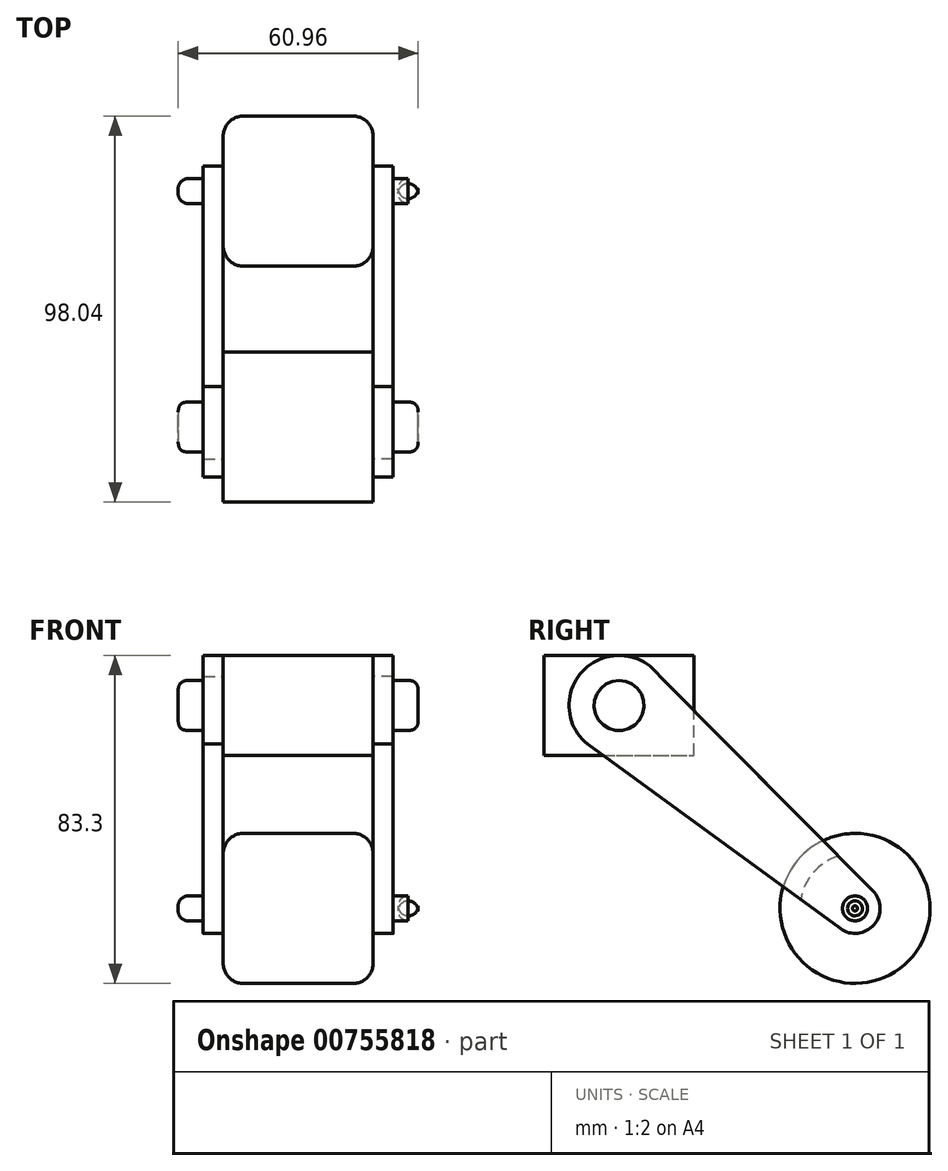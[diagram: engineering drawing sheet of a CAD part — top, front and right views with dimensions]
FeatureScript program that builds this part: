
annotation { "Feature Type Name" : "Feature", "Feature Type Description" : "" }
export const myFeature = defineFeature(function(context is Context, id is Id, definition is map)
    precondition{}
    {
        {
            var Q0;
            Q0=qCreatedBy(makeId("Right.planeOp"),FACE);
            var sketch = newSketch(context, id + "F0", { "sketchPlane" : qUnion([Q0])});
            skLineSegment(sketch, "E0.bottom", {"start": v(-59, 38.85) * mm, "end": v(-20.9, 38.85) * mm});
            skLineSegment(sketch, "E0.top", {"start": v(-59, 64.25) * mm, "end": v(-20.9, 64.25) * mm});
            skLineSegment(sketch, "E0.left", {"start": v(-59, 38.85) * mm, "end": v(-59, 64.25) * mm});
            skLineSegment(sketch, "E0.right", {"start": v(-20.9, 38.85) * mm, "end": v(-20.9, 64.25) * mm});
            skSolve(sketch);
        }
        {
            var Q0;
            Q0=makeQuery(id+"F0.imprint","IMPRINT",FACE,{"disambiguationData":[TD([[makeQuery(id+"F0.imprint","IMPRINT",EDGE,{"derivedFrom":sQuery(id+"F0.wireOp",EDGE,"E0.bottom")}),1.0]])]});
            extrude(context, id + "F1", {"entities" : qUnion([Q0]), "depth" : 19.05 * mm, "hasSecondDirection" : true, "secondDirectionOppositeDirection" : true, "secondDirectionDepth" : 19.05 * mm});
        }
        {
            var Q0;
            Q0=makeQuery(id+"F1.opExtrude","CAP_FACE",FACE,{"disambiguationData":[OSD([sQuery(id+"F0.wireOp",EDGE,"E0.bottom"),sQuery(id+"F0.wireOp",EDGE,"E0.top"),sQuery(id+"F0.wireOp",EDGE,"E0.left"),sQuery(id+"F0.wireOp",EDGE,"E0.right")])],"isStart":false});
            var sketch = newSketch(context, id + "F2", { "sketchPlane" : qUnion([Q0])});
            skArc(sketch, "E1", {"start": v(-29.6, 58.92) * mm, "mid": v(-48.61, 60.84) * mm, "end": v(-48.03, 41.75) * mm});
            skPoint(sketch, "E1.centerSnap0", {"position": v(-59, 51.55) * mm});
            skPoint(sketch, "E1.centerSnap1", {"position": v(-39.95, 38.85) * mm});
            skArc(sketch, "E2", {"start": v(16.24, -5.14) * mm, "mid": v(24.82, -4.14) * mm, "end": v(24.5, 4.48) * mm});
            skLineSegment(sketch, "E3", {"start": v(-29.6, 58.92) * mm, "end": v(24.5, 4.48) * mm});
            skLineSegment(sketch, "E4", {"start": v(-48.03, 41.75) * mm, "end": v(16.24, -5.14) * mm});
            skCircle(sketch, "E5", {"center": v(20, 0) * mm, "radius": 3.18 * mm});
            skSolve(sketch);
        }
        {
            var Q0;
            Q0=qSketchRegion(id+"F2",true);
            extrude(context, id + "F3", {"entities" : qUnion([Q0]), "depth" : 5.08 * mm});
        }
        {
            var Q0;
            Q0=makeQuery(id+"F3.opExtrude","CAP_FACE",FACE,{"disambiguationData":[OSD([sQuery(id+"F2.wireOp",EDGE,"E1"),sQuery(id+"F2.wireOp",EDGE,"E2"),sQuery(id+"F2.wireOp",EDGE,"E3"),sQuery(id+"F2.wireOp",EDGE,"E4")])],"isStart":true});
            cPlane(context, id + "F4", {"entities" : qUnion([Q0]), "cplaneType" : CPlaneType.OFFSET, "offset" : 19.05 * mm, "width" : 152.4 * mm, "height" : 152.4 * mm});
        }
        {
            var Q0;
            Q0=makeQuery(id+"F3.opExtrude","SWEPT_BODY",BODY,{"disambiguationData":[OSD([sQuery(id+"F2.wireOp",EDGE,"E1"),sQuery(id+"F2.wireOp",EDGE,"E2"),sQuery(id+"F2.wireOp",EDGE,"E3"),sQuery(id+"F2.wireOp",EDGE,"E4")])]});
            var Q1;
            Q1=qCreatedBy(id+"F4.planeOp",FACE);
            mirror(context, id + "F5", {"entities" : qUnion([Q0]), "mirrorPlane" : qUnion([Q1])});
        }
        {
            var Q0;
            Q0=makeQuery(id+"F3.opExtrude","CAP_FACE",FACE,{"disambiguationData":[OSD([sQuery(id+"F2.wireOp",EDGE,"E1"),sQuery(id+"F2.wireOp",EDGE,"E2"),sQuery(id+"F2.wireOp",EDGE,"E3"),sQuery(id+"F2.wireOp",EDGE,"E4")])],"isStart":true});
            var sketch = newSketch(context, id + "F6", { "sketchPlane" : qUnion([Q0])});
            skCircle(sketch, "E6", {"center": v(-20, 0) * mm, "radius": 19.05 * mm});
            skCircle(sketch, "E7", {"center": v(-20, 0) * mm, "radius": 3.18 * mm});
            skSolve(sketch);
        }
        {
            var Q0;
            Q0=qSketchRegion(id+"F6",true);
            extrude(context, id + "F7", {"entities" : qUnion([Q0]), "depth" : 38.1 * mm});
        }
        {
            var Q0;
            Q0=makeQuery(id+"F5.opPattern","COPY",FACE,{"derivedFrom":makeQuery(id+"F3.opExtrude","CAP_FACE",FACE,{"disambiguationData":[OSD([sQuery(id+"F2.wireOp",EDGE,"E1"),sQuery(id+"F2.wireOp",EDGE,"E2"),sQuery(id+"F2.wireOp",EDGE,"E3"),sQuery(id+"F2.wireOp",EDGE,"E4")])],"isStart":false}),"instanceName":"1"});
            var sketch = newSketch(context, id + "F8", { "sketchPlane" : qUnion([Q0])});
            skCircle(sketch, "E8", {"center": v(39.95, 51.55) * mm, "radius": 6.35 * mm});
            skSolve(sketch);
        }
        {
            var Q0;
            Q0=qSketchRegion(id+"F8",true);
            extrude(context, id + "F9", {"entities" : qUnion([Q0]), "depth" : 6.35 * mm});
        }
        {
            var Q0;
            Q0=makeQuery(id+"F9.opExtrude","CAP_FACE",FACE,{"disambiguationData":[OSD([sQuery(id+"F8.wireOp",EDGE,"E8")])],"isStart":false});
            fillet(context, id + "F10", {"entities" : qUnion([Q0]), "radius" : 2.54 * mm, "tangentPropagation" : true, "rho" : 0.5, "crossSection" : FilletCrossSection.CONIC, "allowEdgeOverflow" : false});
        }
        {
            var Q0;
            Q0=makeQuery(id+"F9.opExtrude","SWEPT_BODY",BODY,{"disambiguationData":[OSD([sQuery(id+"F8.wireOp",EDGE,"E8")])]});
            var Q1;
            Q1=qCreatedBy(id+"F4.planeOp",FACE);
            mirror(context, id + "F11", {"entities" : qUnion([Q0]), "mirrorPlane" : qUnion([Q1])});
        }
        {
            var Q0;
            Q0=makeQuery(id+"F7.opExtrude","CAP_EDGE",EDGE,{"disambiguationData":[OSD([sQuery(id+"F6.wireOp",EDGE,"E6")])],"isStart":true});
            fillet(context, id + "F12", {"entities" : qUnion([Q0]), "radius" : 5.08 * mm, "tangentPropagation" : true, "allowEdgeOverflow" : false});
        }
        {
            var Q0;
            Q0=makeQuery(id+"F7.opExtrude","CAP_EDGE",EDGE,{"disambiguationData":[OSD([sQuery(id+"F6.wireOp",EDGE,"E6")])],"isStart":false});
            fillet(context, id + "F13", {"entities" : qUnion([Q0]), "radius" : 5.08 * mm, "tangentPropagation" : true, "allowEdgeOverflow" : false});
        }
        {
            var Q0;
            Q0=makeQuery(id+"F5.opPattern","COPY",FACE,{"derivedFrom":makeQuery(id+"F3.opExtrude","CAP_FACE",FACE,{"disambiguationData":[OSD([sQuery(id+"F2.wireOp",EDGE,"E1"),sQuery(id+"F2.wireOp",EDGE,"E2"),sQuery(id+"F2.wireOp",EDGE,"E3"),sQuery(id+"F2.wireOp",EDGE,"E4"),sQuery(id+"F2.wireOp",EDGE,"E5")])],"isStart":false}),"instanceName":"1"});
            var sketch = newSketch(context, id + "F14", { "sketchPlane" : qUnion([Q0])});
            skCircle(sketch, "E9", {"center": v(-20, 0) * mm, "radius": 3.18 * mm});
            skSolve(sketch);
        }
        {
            var Q0;
            Q0=qSketchRegion(id+"F14",true);
            extrude(context, id + "F15", {"entities" : qUnion([Q0]), "operationType" : NewBodyOperationType.ADD, "depth" : 6.35 * mm, "hasSecondDirection" : true, "secondDirectionOppositeDirection" : true, "secondDirectionDepth" : 54.6 * mm});
        }
        {
            var Q0;
            Q0=makeQuery(id+"F15.opExtrude","CAP_EDGE",EDGE,{"disambiguationData":[OSD([sQuery(id+"F14.wireOp",EDGE,"E9")])],"isStart":true});
            fillet(context, id + "F16", {"entities" : qUnion([Q0]), "radius" : 2.54 * mm, "tangentPropagation" : true, "allowEdgeOverflow" : false});
        }
        {
            var Q0;
            Q0=makeQuery(id+"F15.opExtrude","CAP_EDGE",EDGE,{"disambiguationData":[OSD([sQuery(id+"F14.wireOp",EDGE,"E9")])],"isStart":false});
            fillet(context, id + "F17", {"entities" : qUnion([Q0]), "radius" : 2.54 * mm, "tangentPropagation" : true, "allowEdgeOverflow" : false});
        }
    });
